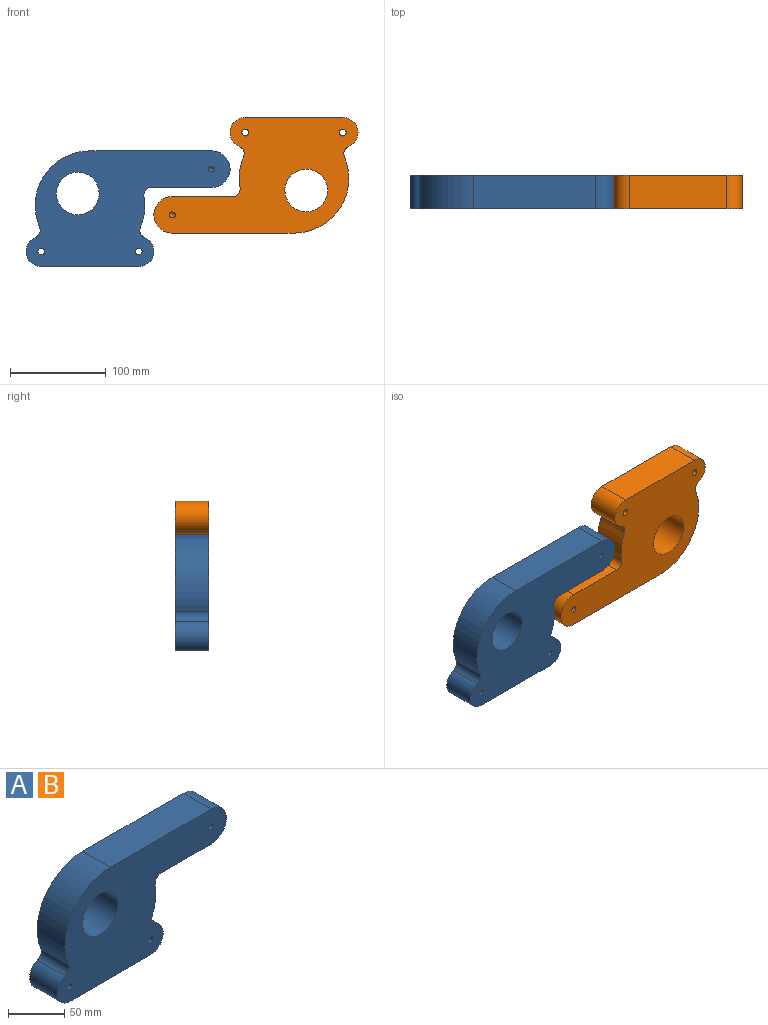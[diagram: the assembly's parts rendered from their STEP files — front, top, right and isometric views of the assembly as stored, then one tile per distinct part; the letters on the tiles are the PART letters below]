
ASSEMBLY  parts=2 mates=1
PART A: 18 faces, bbox 212.7x34.9x120.7 mm
  f0: cylinder r=57.15mm len=79.63mm, axis (0,1,0), area 3942mm2, adj f1,f12,f14,f15
  f1: cylinder r=7.94mm len=34.93mm, axis (0,1,0), area 439.5mm2, adj f0,f2,f14,f15
  f2: cylinder r=15.88mm len=34.93mm, axis (0,1,0), area 1525.8mm2, adj f1,f3,f14,f15
  f3: plane 101.6x34.93mm, normal (0,0,-1), area 3548.4mm2, adj f2,f4,f14,f15
  f4: cylinder r=15.88mm len=34.93mm, axis (0,1,0), area 1525.8mm2, adj f3,f5,f14,f15
  f5: cylinder r=7.94mm len=34.93mm, axis (0,1,0), area 439.5mm2, adj f4,f6,f14,f15
  f6: cylinder r=57.15mm len=34.93mm, axis (0,1,0), area 1149.2mm2, adj f5,f7,f14,f15
  f7: cylinder r=7.94mm len=34.93mm, axis (0,1,0), area 483mm2, adj f6,f8,f14,f15
  f8: plane 62.87x34.93mm, normal (0,0,-1), area 2195.7mm2, adj f7,f9,f14,f15
  f9: cylinder r=19.05mm len=38.1mm, axis (0,1,0), area 2090.2mm2, adj f8,f12,f14,f15
  f10: cylinder r=3.57mm len=34.93mm, axis (0,1,0), area 783.8mm2, adj f14,f15
  f11: cylinder r=22.23mm len=44.45mm, axis (0,1,0), area 4877.1mm2, adj f14,f15
  f12: plane 127x34.93mm, normal (0,0,1), area 4435.5mm2, adj f0,f9,f14,f15
  f13: cylinder r=3.57mm len=34.93mm, axis (0,1,0), area 783.8mm2, adj f14,f15
  f14: plane 212.73x120.65mm, normal (0,-1,0), area 14896.8mm2, adj f0,f1,f2,f3,f4,f5,f6,f7
  f15: plane 212.73x120.65mm, normal (0,1,0), area 14928.4mm2, adj f0,f1,f2,f3,f4,f5,f6,f7
  f16: cone r=0mm half-angle=59deg, axis (0,-1,0), area 36.9mm2, adj f17
  f17: cylinder r=3.17mm len=12.7mm, axis (0,-1,0), area 253.4mm2, adj f14,f16
PART B: same geometry as A
PLACE A t=(12.7,34.93,-76.2)mm
PLACE B rot(axis=(0,1,0),180deg) t=(225.42,34.93,79.38)mm
MATE fastened B.f9 <-> A.f14  axis (0,-1,0) through (98.43,0,-22.22)mm
